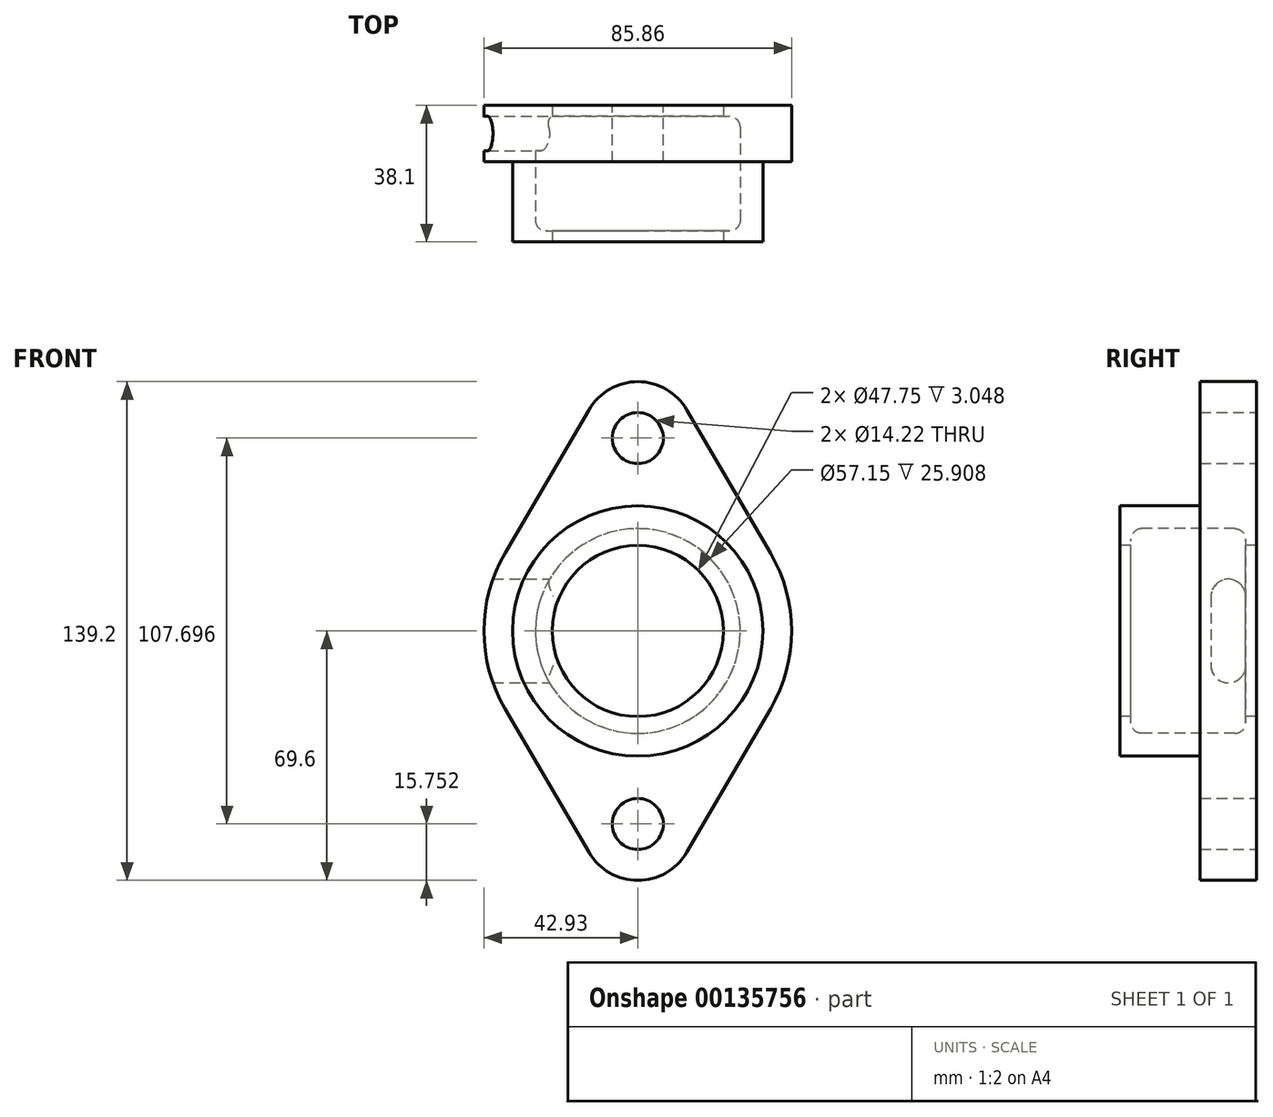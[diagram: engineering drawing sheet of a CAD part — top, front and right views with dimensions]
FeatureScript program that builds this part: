
annotation { "Feature Type Name" : "Feature", "Feature Type Description" : "" }
export const myFeature = defineFeature(function(context is Context, id is Id, definition is map)
    precondition{}
    {
        {
            var Q0;
            Q0=qCreatedBy(makeId("Front.planeOp"),FACE);
            var sketch = newSketch(context, id + "F0", { "sketchPlane" : qUnion([Q0])});
            skLineSegment(sketch, "E0", {"start": v(-39.2, 0) * mm, "end": v(39.73, 0) * mm, "construction": true});
            skLineSegment(sketch, "E1", {"start": v(0, 79.16) * mm, "end": v(0, -73.29) * mm, "construction": true});
            skLineSegment(sketch, "E2", {"start": v(-13.6, 61.8) * mm, "end": v(-37.06, 21.67) * mm});
            skLineSegment(sketch, "E3", {"start": v(13.6, 61.8) * mm, "end": v(37.06, 21.67) * mm});
            skLineSegment(sketch, "E4", {"start": v(-37.06, -21.67) * mm, "end": v(-13.6, -61.8) * mm});
            skLineSegment(sketch, "E5", {"start": v(37.06, -21.67) * mm, "end": v(13.6, -61.8) * mm});
            skArc(sketch, "E6", {"start": v(13.6, 61.8) * mm, "mid": v(0, 69.6) * mm, "end": v(-13.6, 61.8) * mm});
            skArc(sketch, "E7", {"start": v(-37.06, 21.67) * mm, "mid": v(-42.93, 0) * mm, "end": v(-37.06, -21.67) * mm});
            skArc(sketch, "E8", {"start": v(37.06, -21.67) * mm, "mid": v(42.93, 0) * mm, "end": v(37.06, 21.67) * mm});
            skArc(sketch, "E9", {"start": v(-13.6, -61.8) * mm, "mid": v(0, -69.6) * mm, "end": v(13.6, -61.8) * mm});
            skCircle(sketch, "E10", {"center": v(0, 53.85) * mm, "radius": 7.11 * mm});
            skCircle(sketch, "E11", {"center": v(0, -53.85) * mm, "radius": 7.11 * mm});
            skSolve(sketch);
        }
        {
            var Q0;
            Q0=makeQuery(id+"F0.imprint","IMPRINT",FACE,{"disambiguationData":[TD([[makeQuery(id+"F0.imprint","IMPRINT",EDGE,{"derivedFrom":sQuery(id+"F0.wireOp",EDGE,"E2")}),1.0]])]});
            extrude(context, id + "F1", {"entities" : qUnion([Q0]), "depth" : 15.75 * mm});
        }
        {
            var Q0;
            Q0=makeQuery(id+"F1.opExtrude","CAP_FACE",FACE,{"disambiguationData":[OSD([sQuery(id+"F0.wireOp",EDGE,"E2"),sQuery(id+"F0.wireOp",EDGE,"E3"),sQuery(id+"F0.wireOp",EDGE,"E4"),sQuery(id+"F0.wireOp",EDGE,"E5"),sQuery(id+"F0.wireOp",EDGE,"E6"),sQuery(id+"F0.wireOp",EDGE,"E7"),sQuery(id+"F0.wireOp",EDGE,"E8"),sQuery(id+"F0.wireOp",EDGE,"E9"),sQuery(id+"F0.wireOp",EDGE,"E10"),sQuery(id+"F0.wireOp",EDGE,"E11")])],"isStart":false});
            var sketch = newSketch(context, id + "F2", { "sketchPlane" : qUnion([Q0])});
            skCircle(sketch, "E12", {"center": v(0, 0) * mm, "radius": 34.93 * mm});
            skSolve(sketch);
        }
        {
            var Q0;
            Q0 = qSketchRegion(id + "F2", true);
            extrude(context, id + "F3", {"entities" : qUnion([Q0]), "operationType" : NewBodyOperationType.ADD, "depth" : 22.35 * mm});
        }
        {
            var Q0;
            Q0=makeQuery(id+"F3.opExtrude","CAP_FACE",FACE,{"disambiguationData":[OSD([sQuery(id+"F2.wireOp",EDGE,"E12")])],"isStart":false});
            var sketch = newSketch(context, id + "F4", { "sketchPlane" : qUnion([Q0])});
            skCircle(sketch, "E13", {"center": v(0, 0) * mm, "radius": 23.88 * mm});
            skSolve(sketch);
        }
        {
            var Q0;
            Q0=makeQuery(id+"F4.imprint","IMPRINT",FACE,{"disambiguationData":[TD([[makeQuery(id+"F4.imprint","IMPRINT",EDGE,{"derivedFrom":sQuery(id+"F4.wireOp",EDGE,"E13")}),1.0]])]});
            extrude(context, id + "F5", {"entities" : qUnion([Q0]), "operationType" : NewBodyOperationType.REMOVE, "endBound" : BoundingType.THROUGH_ALL, "oppositeDirection" : true, "depth" : 25.4 * mm});
        }
        {
            var Q0;
            Q0=qCreatedBy(makeId("Right.planeOp"),FACE);
            var sketch = newSketch(context, id + "F6", { "sketchPlane" : qUnion([Q0])});
            skLineSegment(sketch, "E14", {"start": v(-3.05, 9.65) * mm, "end": v(-3.05, -9.65) * mm});
            skLineSegment(sketch, "E15", {"start": v(-12.7, 9.65) * mm, "end": v(-12.7, -9.65) * mm});
            skArc(sketch, "E16", {"start": v(-3.05, 9.65) * mm, "mid": v(-7.87, 14.48) * mm, "end": v(-12.7, 9.65) * mm});
            skArc(sketch, "E17", {"start": v(-12.7, -9.65) * mm, "mid": v(-7.87, -14.48) * mm, "end": v(-3.05, -9.65) * mm});
            skSolve(sketch);
        }
        {
            var Q0;
            Q0 = qSketchRegion(id + "F6", true);
            extrude(context, id + "F7", {"entities" : qUnion([Q0]), "operationType" : NewBodyOperationType.REMOVE, "endBound" : BoundingType.THROUGH_ALL, "oppositeDirection" : true, "depth" : 25.4 * mm});
        }
        {
            var Q0;
            Q0=qCreatedBy(makeId("Top.planeOp"),FACE);
            var sketch = newSketch(context, id + "F8", { "sketchPlane" : qUnion([Q0])});
            skLineSegment(sketch, "E18", {"start": v(0, -3.05) * mm, "end": v(0, -35.05) * mm});
            skLineSegment(sketch, "E19", {"start": v(0, -35.05) * mm, "end": v(-25.53, -35.05) * mm});
            skLineSegment(sketch, "E20", {"start": v(-28.58, -32) * mm, "end": v(-28.58, -6.1) * mm});
            skLineSegment(sketch, "E21", {"start": v(-25.53, -3.05) * mm, "end": v(0, -3.05) * mm});
            skPoint(sketch, "E22.visualSharp", {"position": v(-28.58, -3.05) * mm});
            skArc(sketch, "E22.filletArc", {"start": v(-25.53, -3.05) * mm, "mid": v(-27.68, -3.94) * mm, "end": v(-28.58, -6.1) * mm});
            skPoint(sketch, "E23.visualSharp", {"position": v(-28.58, -35.05) * mm});
            skArc(sketch, "E23.filletArc", {"start": v(-28.58, -32) * mm, "mid": v(-27.68, -34.16) * mm, "end": v(-25.53, -35.05) * mm});
            skLineSegment(sketch, "E24", {"start": v(0, 16.1) * mm, "end": v(0, -43.74) * mm, "construction": true});
            skSolve(sketch);
        }
        {
            var Q0;
            Q0=makeQuery(id+"F8.imprint","IMPRINT",FACE,{"disambiguationData":[TD([[makeQuery(id+"F8.imprint","IMPRINT",EDGE,{"derivedFrom":sQuery(id+"F8.wireOp",EDGE,"E18")}),-1.0]])]});
            var Q1;
            Q1=sQuery(id+"F8.wireOp",EDGE,"E24");
            revolve(context, id + "F9", {"operationType" : NewBodyOperationType.REMOVE, "entities" : qUnion([Q0]), "axis" : qUnion([Q1]), "revolveType" : RevolveType.FULL, "oppositeDirection" : true});
        }
    });
